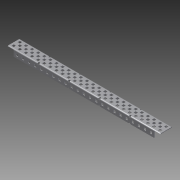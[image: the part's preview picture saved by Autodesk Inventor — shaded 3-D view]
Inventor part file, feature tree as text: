
AUTODESK INVENTOR PART (.ipt)
format: ipt  version: 2012 (Build 160160000, 160)  size: 1,675,776 bytes
history: native  units: in
note: dims shown in document units (in); Inventor stores cm internally (conversion verified against a paired STEP export)
features: sketch x3, extrude x2, other x1, imported_body x1
ambient origin geometry x8: Origin, YZ Plane, XZ Plane, XY Plane, X Axis, Y Axis, Z Axis, Center Point
feature tree (7):
  parser-record x1  (decoder bookkeeping rows leaked as tree rows — omitted from the tree; the rows remain in map.json)
  imported_body  "Base1"
  sketch  "Sketch2"  dims[d5=1.0in d6=0.5in d7=0.0in d8=0.0in d9=1.0in d10=1.5in d11=0.0in d12=0.0in]
  extrude  "Extrusion2"  Depth=1.0in TaperAngle=0.0deg
  extrude  "Extrusion3"  [1 undecoded]
  sketch  "Sketch3"
  sketch  "Sketch4"
note: 1 required parameter value undecoded (feature->parameter linkage not recoverable at this tier; creation-order binding heuristic only, values carry confidence <= 0.55)
